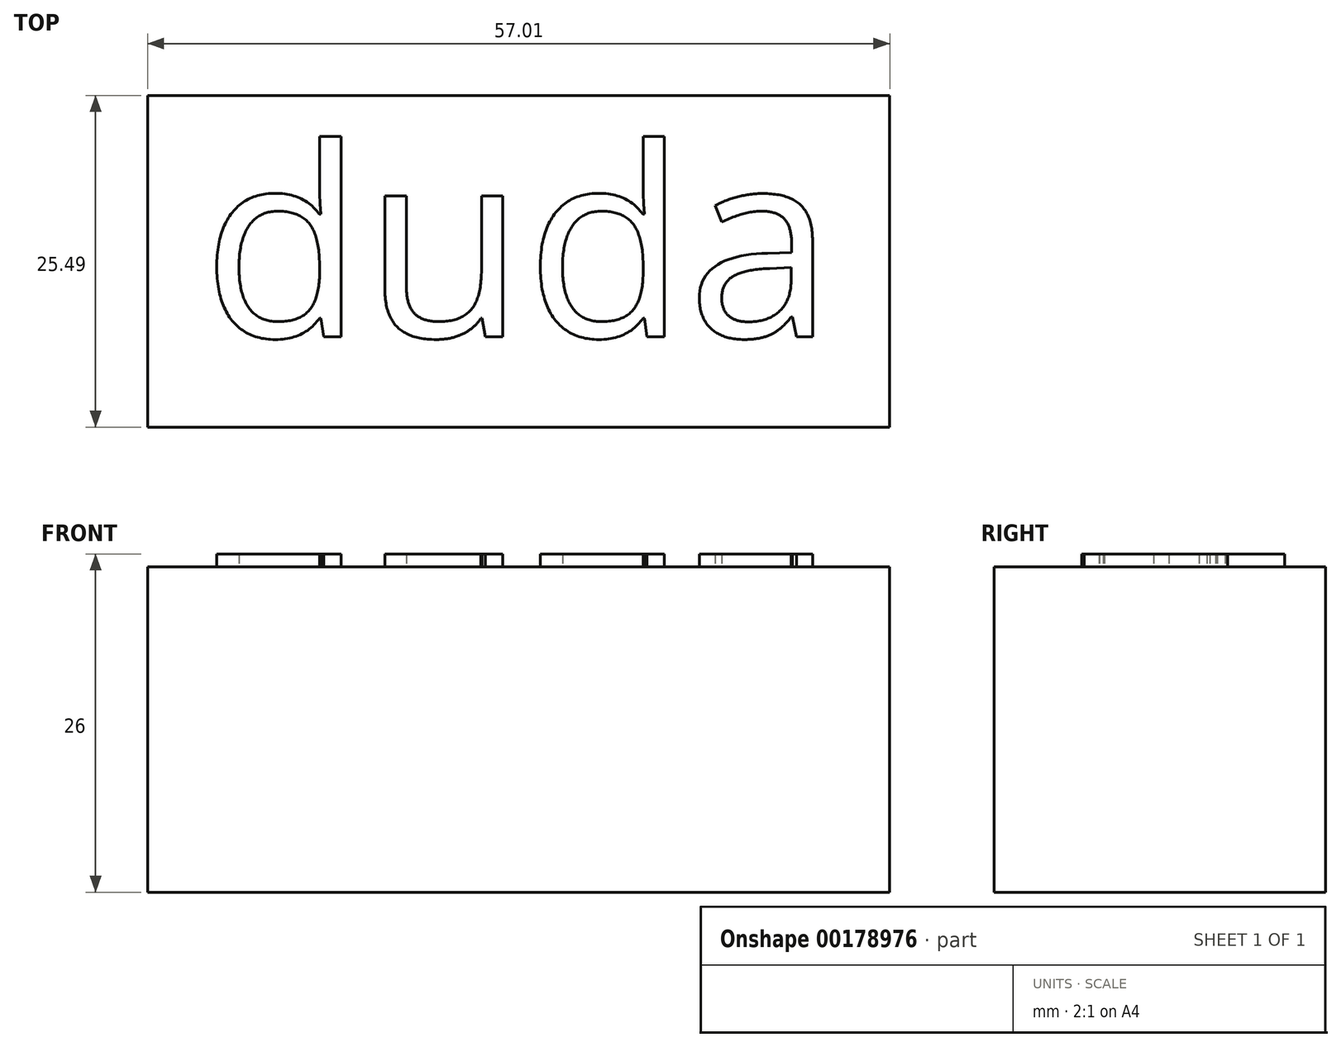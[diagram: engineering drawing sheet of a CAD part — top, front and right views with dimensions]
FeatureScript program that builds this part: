
annotation { "Feature Type Name" : "Feature", "Feature Type Description" : "" }
export const myFeature = defineFeature(function(context is Context, id is Id, definition is map)
    precondition{}
    {
        {
            var Q0;
            Q0=qCreatedBy(makeId("Top.planeOp"),FACE);
            var sketch = newSketch(context, id + "F0", { "sketchPlane" : qUnion([Q0])});
            skLineSegment(sketch, "E0.bottom", {"start": v(-25.67, 10.55) * mm, "end": v(31.34, 10.55) * mm});
            skLineSegment(sketch, "E0.top", {"start": v(-25.67, -14.94) * mm, "end": v(31.34, -14.94) * mm});
            skLineSegment(sketch, "E0.left", {"start": v(-25.67, 10.55) * mm, "end": v(-25.67, -14.94) * mm});
            skLineSegment(sketch, "E0.right", {"start": v(31.34, 10.55) * mm, "end": v(31.34, -14.94) * mm});
            skSolve(sketch);
        }
        {
            var Q0;
            Q0=makeQuery(id+"F0.imprint","IMPRINT",FACE,{"disambiguationData":[TD([[makeQuery(id+"F0.imprint","IMPRINT",EDGE,{"derivedFrom":sQuery(id+"F0.wireOp",EDGE,"E0.bottom")}),-1.0]])]});
            extrude(context, id + "F1", {"entities" : qUnion([Q0]), "depth" : 25 * mm});
        }
        {
            var Q0;
            Q0=makeQuery(id+"F1.opExtrude","CAP_FACE",FACE,{"disambiguationData":[OSD([sQuery(id+"F0.wireOp",EDGE,"E0.bottom"),sQuery(id+"F0.wireOp",EDGE,"E0.top"),sQuery(id+"F0.wireOp",EDGE,"E0.left"),sQuery(id+"F0.wireOp",EDGE,"E0.right")])],"isStart":false});
            var sketch = newSketch(context, id + "F2", { "sketchPlane" : qUnion([Q0])});
            skText(sketch, "E1", { "text": "duda", "fontName": "OpenSans-Regular.ttf"});
            const initialGuessF2  = {"E1": [-0.0215, -0.00801, 1, 0, 0.01459]};
            skSetInitialGuess(sketch, initialGuessF2);
            skSolve(sketch);
        }
        {
            var Q0;
            Q0 = qSketchRegion(id + "F2", true);
            extrude(context, id + "F3", {"entities" : qUnion([Q0]), "operationType" : NewBodyOperationType.ADD, "depth" : 1 * mm});
        }
    });
